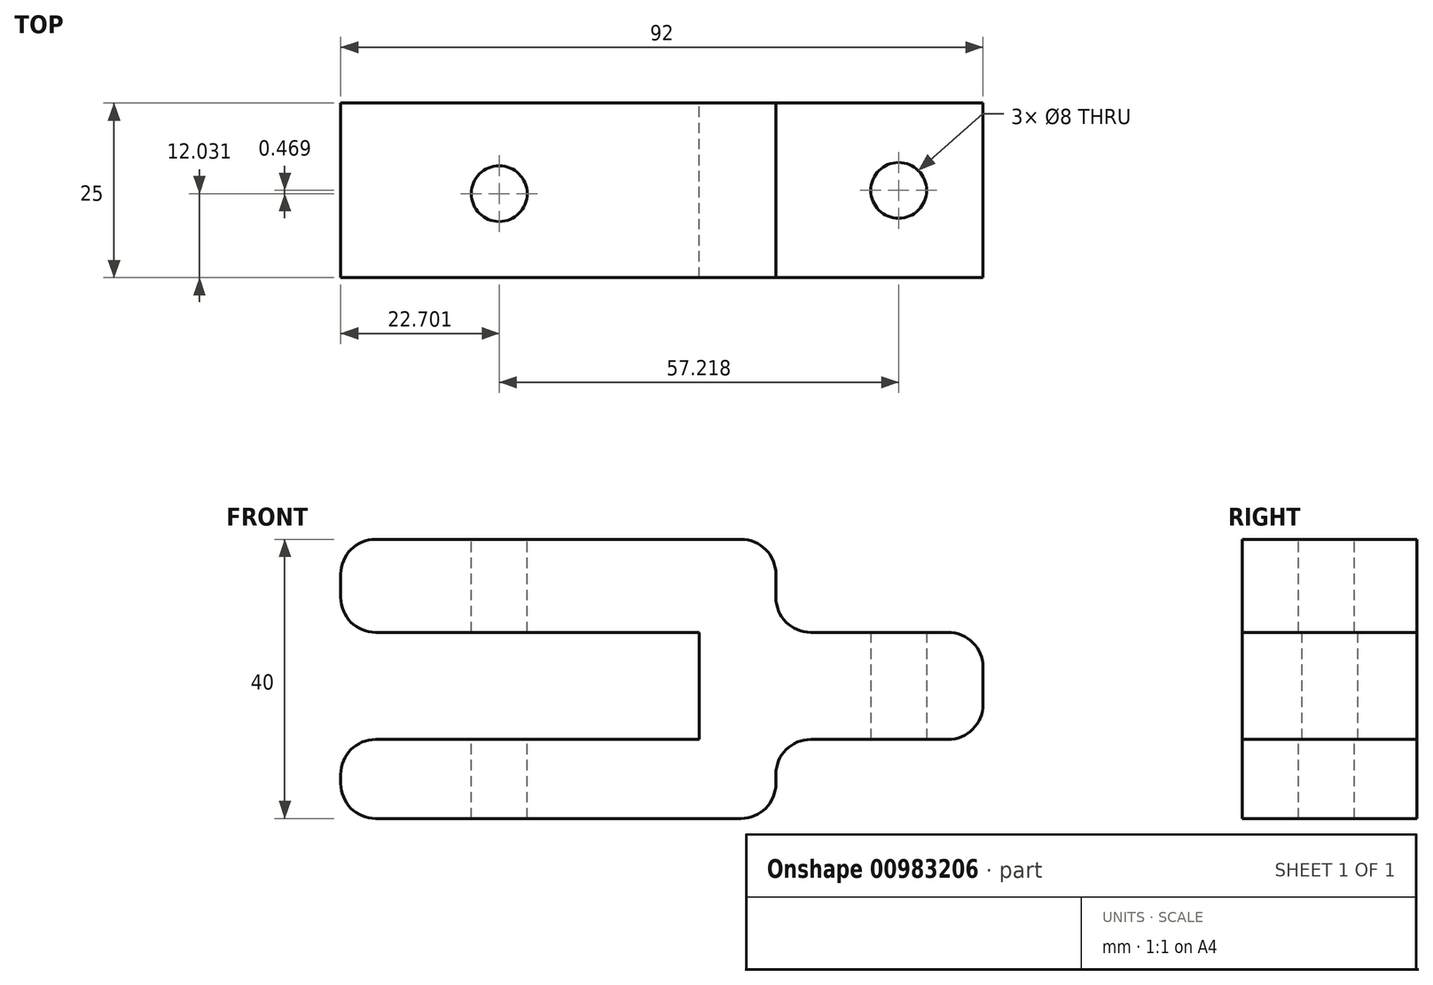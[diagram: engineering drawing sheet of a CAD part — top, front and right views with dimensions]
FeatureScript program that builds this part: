
annotation { "Feature Type Name" : "Feature", "Feature Type Description" : "" }
export const myFeature = defineFeature(function(context is Context, id is Id, definition is map)
    precondition{}
    {
        {
            var Q0;
            Q0=qCreatedBy(makeId("Front.planeOp"),FACE);
            var sketch = newSketch(context, id + "F0", { "sketchPlane" : qUnion([Q0])});
            skLineSegment(sketch, "E0.bottom", {"start": v(0, 0) * mm, "end": v(51.33, 0) * mm});
            skLineSegment(sketch, "E0.top", {"start": v(0, 11.33) * mm, "end": v(51.33, 11.33) * mm});
            skLineSegment(sketch, "E0.left", {"start": v(0, 0) * mm, "end": v(0, 11.33) * mm});
            skLineSegment(sketch, "E0.right", {"start": v(51.33, 0) * mm, "end": v(51.33, 11.33) * mm});
            skLineSegment(sketch, "E1.bottom", {"start": v(51.33, 0) * mm, "end": v(62.33, 0) * mm});
            skLineSegment(sketch, "E1.top", {"start": v(51.33, 40) * mm, "end": v(62.33, 40) * mm});
            skLineSegment(sketch, "E1.left", {"start": v(51.33, 0) * mm, "end": v(51.33, 40) * mm});
            skLineSegment(sketch, "E1.right", {"start": v(62.33, 0) * mm, "end": v(62.33, 40) * mm});
            skLineSegment(sketch, "E2.bottom", {"start": v(51.33, 40) * mm, "end": v(0, 40) * mm});
            skLineSegment(sketch, "E2.top", {"start": v(51.33, 26.67) * mm, "end": v(0, 26.67) * mm});
            skLineSegment(sketch, "E2.left", {"start": v(51.33, 40) * mm, "end": v(51.33, 26.67) * mm});
            skLineSegment(sketch, "E2.right", {"start": v(0, 40) * mm, "end": v(0, 26.67) * mm});
            skLineSegment(sketch, "E3.bottom", {"start": v(62.33, 26.67) * mm, "end": v(92, 26.67) * mm});
            skLineSegment(sketch, "E3.top", {"start": v(62.33, 11.33) * mm, "end": v(92, 11.33) * mm});
            skLineSegment(sketch, "E3.left", {"start": v(62.33, 26.67) * mm, "end": v(62.33, 11.33) * mm});
            skLineSegment(sketch, "E3.right", {"start": v(92, 26.67) * mm, "end": v(92, 11.33) * mm});
            skLineSegment(sketch, "E4.bottom", {"start": v(16.33, 26.67) * mm, "end": v(34.5, 26.67) * mm});
            skLineSegment(sketch, "E4.top", {"start": v(16.33, 25.67) * mm, "end": v(34.5, 25.67) * mm});
            skLineSegment(sketch, "E4.left", {"start": v(16.33, 26.67) * mm, "end": v(16.33, 25.67) * mm});
            skLineSegment(sketch, "E4.right", {"start": v(34.5, 26.67) * mm, "end": v(34.5, 25.67) * mm});
            skLineSegment(sketch, "E5.bottom", {"start": v(16.5, 11.33) * mm, "end": v(34.5, 11.33) * mm});
            skLineSegment(sketch, "E5.top", {"start": v(16.5, 12.33) * mm, "end": v(34.5, 12.33) * mm});
            skLineSegment(sketch, "E5.left", {"start": v(16.5, 11.33) * mm, "end": v(16.5, 12.33) * mm});
            skLineSegment(sketch, "E5.right", {"start": v(34.5, 11.33) * mm, "end": v(34.5, 12.33) * mm});
            skSolve(sketch);
        }
        {
            var Q0;
            Q0=makeQuery(id+"F0.imprint","IMPRINT",FACE,{"disambiguationData":[TD([[makeQuery(id+"F0.imprint","IMPRINT",EDGE,{"derivedFrom":sQuery(id+"F0.wireOp",EDGE,"E4.bottom")}),-1.0]])]});
            var Q1;
            Q1=makeQuery(id+"F0.imprint","IMPRINT",FACE,{"disambiguationData":[TD([[makeQuery(id+"F0.imprint","IMPRINT",EDGE,{"derivedFrom":sQuery(id+"F0.wireOp",EDGE,"E2.bottom")}),1.0]])]});
            var Q2;
            {var subQ3=sQuery(id+"F0.wireOp",EDGE,"E1.bottom");Q2=makeQuery(id+"F0.imprint","IMPRINT",FACE,{"disambiguationData":[TD([[makeQuery(id+"F0.imprint","IMPRINT",EDGE,{"derivedFrom":subQ3}),1.0]])]});}
            var Q3;
            Q3=makeQuery(id+"F0.imprint","IMPRINT",FACE,{"disambiguationData":[TD([[makeQuery(id+"F0.imprint","IMPRINT",EDGE,{"derivedFrom":sQuery(id+"F0.wireOp",EDGE,"E3.bottom")}),-1.0]])]});
            var Q4;
            {var subQ5=sQuery(id+"F0.wireOp",EDGE,"E0.bottom");Q4=makeQuery(id+"F0.imprint","IMPRINT",FACE,{"disambiguationData":[TD([[makeQuery(id+"F0.imprint","IMPRINT",EDGE,{"derivedFrom":subQ5}),1.0]])]});}
            var Q5;
            Q5=makeQuery(id+"F0.imprint","IMPRINT",FACE,{"disambiguationData":[TD([[makeQuery(id+"F0.imprint","IMPRINT",EDGE,{"derivedFrom":sQuery(id+"F0.wireOp",EDGE,"E5.bottom")}),1.0]])]});
            extrude(context, id + "F1", {"entities" : qUnion([Q0, Q1, Q2, Q3, Q4, Q5]), "depth" : 25 * mm, "offsetDistance" : 25 * mm});
        }
        {
            var Q0;
            Q0=makeQuery(id+"F1.opExtrude","SWEPT_EDGE",EDGE,{"disambiguationData":[OSD([sQuery(id+"F0.wireOp",EDGE,"E1.top"),sQuery(id+"F0.wireOp",EDGE,"E1.right")])]});
            fillet(context, id + "F2", {"entities" : qUnion([Q0]), "radius" : 5 * mm, "tangentPropagation" : true, "allowEdgeOverflow" : false});
        }
        {
            var Q0;
            Q0=makeQuery(id+"F1.opExtrude","SWEPT_EDGE",EDGE,{"disambiguationData":[OSD([sQuery(id+"F0.wireOp",EDGE,"E1.right"),sQuery(id+"F0.wireOp",EDGE,"E3.bottom"),sQuery(id+"F0.wireOp",EDGE,"E3.left")])]});
            fillet(context, id + "F3", {"entities" : qUnion([Q0]), "radius" : 5 * mm, "tangentPropagation" : true, "allowEdgeOverflow" : false});
        }
        {
            var Q0;
            Q0=makeQuery(id+"F1.opExtrude","SWEPT_EDGE",EDGE,{"disambiguationData":[OSD([sQuery(id+"F0.wireOp",EDGE,"E3.bottom"),sQuery(id+"F0.wireOp",EDGE,"E3.right")])]});
            fillet(context, id + "F4", {"entities" : qUnion([Q0]), "radius" : 5 * mm, "tangentPropagation" : true, "allowEdgeOverflow" : false});
        }
        {
            var Q0;
            Q0=makeQuery(id+"F1.opExtrude","SWEPT_EDGE",EDGE,{"disambiguationData":[OSD([sQuery(id+"F0.wireOp",EDGE,"E2.bottom"),sQuery(id+"F0.wireOp",EDGE,"E2.right")])]});
            fillet(context, id + "F5", {"entities" : qUnion([Q0]), "radius" : 5 * mm, "tangentPropagation" : true, "allowEdgeOverflow" : false});
        }
        {
            var Q0;
            Q0=makeQuery(id+"F1.opExtrude","SWEPT_EDGE",EDGE,{"disambiguationData":[OSD([sQuery(id+"F0.wireOp",EDGE,"E2.top"),sQuery(id+"F0.wireOp",EDGE,"E2.right")])]});
            fillet(context, id + "F6", {"entities" : qUnion([Q0]), "radius" : 5 * mm, "tangentPropagation" : true, "allowEdgeOverflow" : false});
        }
        {
            var Q0;
            Q0=makeQuery(id+"F1.opExtrude","SWEPT_EDGE",EDGE,{"disambiguationData":[OSD([sQuery(id+"F0.wireOp",EDGE,"E0.top"),sQuery(id+"F0.wireOp",EDGE,"E0.left")])]});
            fillet(context, id + "F7", {"entities" : qUnion([Q0]), "radius" : 5 * mm, "tangentPropagation" : true, "allowEdgeOverflow" : false});
        }
        {
            var Q0;
            Q0=makeQuery(id+"F1.opExtrude","SWEPT_EDGE",EDGE,{"disambiguationData":[OSD([sQuery(id+"F0.wireOp",EDGE,"E0.bottom"),sQuery(id+"F0.wireOp",EDGE,"E0.left")])]});
            fillet(context, id + "F8", {"entities" : qUnion([Q0]), "radius" : 5 * mm, "tangentPropagation" : true, "allowEdgeOverflow" : false});
        }
        {
            var Q0;
            Q0=makeQuery(id+"F1.opExtrude","SWEPT_EDGE",EDGE,{"disambiguationData":[OSD([sQuery(id+"F0.wireOp",EDGE,"E1.bottom"),sQuery(id+"F0.wireOp",EDGE,"E1.right")])]});
            fillet(context, id + "F9", {"entities" : qUnion([Q0]), "radius" : 5 * mm, "tangentPropagation" : true, "allowEdgeOverflow" : false});
        }
        {
            var Q0;
            Q0=makeQuery(id+"F1.opExtrude","SWEPT_EDGE",EDGE,{"disambiguationData":[OSD([sQuery(id+"F0.wireOp",EDGE,"E1.right"),sQuery(id+"F0.wireOp",EDGE,"E3.top"),sQuery(id+"F0.wireOp",EDGE,"E3.left")])]});
            fillet(context, id + "F10", {"entities" : qUnion([Q0]), "radius" : 5 * mm, "tangentPropagation" : true, "allowEdgeOverflow" : false});
        }
        {
            var Q0;
            Q0=makeQuery(id+"F1.opExtrude","SWEPT_EDGE",EDGE,{"disambiguationData":[OSD([sQuery(id+"F0.wireOp",EDGE,"E3.top"),sQuery(id+"F0.wireOp",EDGE,"E3.right")])]});
            fillet(context, id + "F11", {"entities" : qUnion([Q0]), "radius" : 5 * mm, "tangentPropagation" : true, "allowEdgeOverflow" : false});
        }
        {
            var Q0;
            Q0=makeQuery(id+"F1.opExtrude","SWEPT_FACE",FACE,{"disambiguationData":[OSD([sQuery(id+"F0.wireOp",EDGE,"E1.top"),sQuery(id+"F0.wireOp",EDGE,"E2.bottom")])]});
            var sketch = newSketch(context, id + "F12", { "sketchPlane" : qUnion([Q0])});
            skPoint(sketch, "E6", {"position": v(22.7, -12.97) * mm});
            skSolve(sketch);
        }
        {
            var Q0;
            Q0=sQuery(id+"F12.wireOp",VERTEX,"E6");
            var Q1;
            Q1=makeQuery(id+"F1.opExtrude","SWEPT_BODY",BODY,{"disambiguationData":[OSD([sQuery(id+"F0.wireOp",EDGE,"E0.bottom"),sQuery(id+"F0.wireOp",EDGE,"E0.top"),sQuery(id+"F0.wireOp",EDGE,"E0.left"),sQuery(id+"F0.wireOp",EDGE,"E1.bottom"),sQuery(id+"F0.wireOp",EDGE,"E1.top"),sQuery(id+"F0.wireOp",EDGE,"E1.left"),sQuery(id+"F0.wireOp",EDGE,"E1.right"),sQuery(id+"F0.wireOp",EDGE,"E2.bottom"),sQuery(id+"F0.wireOp",EDGE,"E2.top"),sQuery(id+"F0.wireOp",EDGE,"E2.right"),sQuery(id+"F0.wireOp",EDGE,"E3.bottom"),sQuery(id+"F0.wireOp",EDGE,"E3.top"),sQuery(id+"F0.wireOp",EDGE,"E3.right"),sQuery(id+"F0.wireOp",EDGE,"E4.top"),sQuery(id+"F0.wireOp",EDGE,"E4.left"),sQuery(id+"F0.wireOp",EDGE,"E4.right"),sQuery(id+"F0.wireOp",EDGE,"E5.top"),sQuery(id+"F0.wireOp",EDGE,"E5.left"),sQuery(id+"F0.wireOp",EDGE,"E5.right")])]});
            hole(context, id + "F13", {"style" : HoleStyle.SIMPLE, "endStyle" : HoleEndStyle.THROUGH, "holeDiameter" : 8 * mm, "majorDiameter" : 5 * mm, "isTappedThrough" : true, "tappedDepth" : 12 * mm, "tapClearance" : 3, "locations" : qUnion([Q0]), "scope" : qUnion([Q1])});
        }
        {
            var Q0;
            Q0=makeQuery(id+"F1.opExtrude","SWEPT_FACE",FACE,{"disambiguationData":[OSD([sQuery(id+"F0.wireOp",EDGE,"E3.top")])]});
            var sketch = newSketch(context, id + "F14", { "sketchPlane" : qUnion([Q0])});
            skPoint(sketch, "E7", {"position": v(79.92, 12.5) * mm});
            skPoint(sketch, "E7.positionSnap0", {"position": v(87, 12.5) * mm});
            skSolve(sketch);
        }
        {
            var Q0;
            Q0=sQuery(id+"F14.wireOp",VERTEX,"E7");
            var Q1;
            Q1=makeQuery(id+"F1.opExtrude","SWEPT_BODY",BODY,{"disambiguationData":[OSD([sQuery(id+"F0.wireOp",EDGE,"E0.bottom"),sQuery(id+"F0.wireOp",EDGE,"E0.top"),sQuery(id+"F0.wireOp",EDGE,"E0.left"),sQuery(id+"F0.wireOp",EDGE,"E1.bottom"),sQuery(id+"F0.wireOp",EDGE,"E1.top"),sQuery(id+"F0.wireOp",EDGE,"E1.left"),sQuery(id+"F0.wireOp",EDGE,"E1.right"),sQuery(id+"F0.wireOp",EDGE,"E2.bottom"),sQuery(id+"F0.wireOp",EDGE,"E2.top"),sQuery(id+"F0.wireOp",EDGE,"E2.right"),sQuery(id+"F0.wireOp",EDGE,"E3.bottom"),sQuery(id+"F0.wireOp",EDGE,"E3.top"),sQuery(id+"F0.wireOp",EDGE,"E3.right"),sQuery(id+"F0.wireOp",EDGE,"E4.top"),sQuery(id+"F0.wireOp",EDGE,"E4.left"),sQuery(id+"F0.wireOp",EDGE,"E4.right"),sQuery(id+"F0.wireOp",EDGE,"E5.top"),sQuery(id+"F0.wireOp",EDGE,"E5.left"),sQuery(id+"F0.wireOp",EDGE,"E5.right")])]});
            hole(context, id + "F15", {"style" : HoleStyle.SIMPLE, "endStyle" : HoleEndStyle.THROUGH, "holeDiameter" : 8 * mm, "majorDiameter" : 5 * mm, "isTappedThrough" : true, "tappedDepth" : 12 * mm, "tapClearance" : 3, "locations" : qUnion([Q0]), "scope" : qUnion([Q1])});
        }
    });
